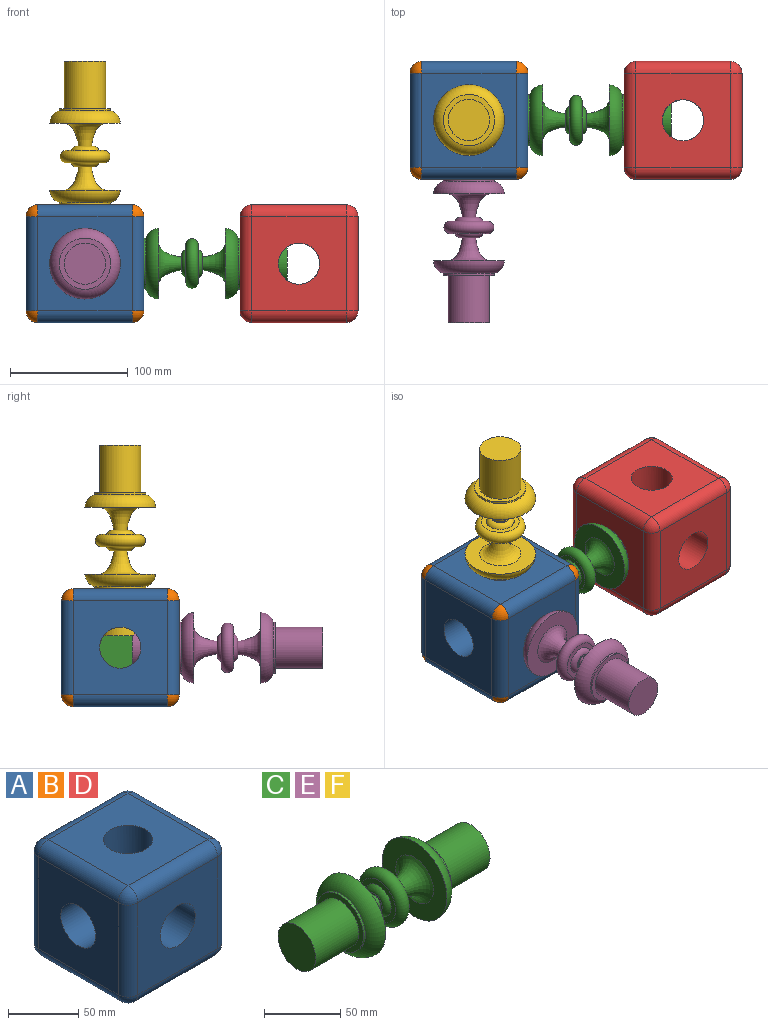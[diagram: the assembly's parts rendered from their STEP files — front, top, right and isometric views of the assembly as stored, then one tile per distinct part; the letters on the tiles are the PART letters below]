
ASSEMBLY  parts=6 mates=4
PART A: 32 faces, bbox 100x100x100 mm
  f0: cylinder r=17.5mm len=37.63mm, axis (0,-1,0), area 3765.4mm2, adj f5,f8,f9,f10,f11
  f1: plane 80x80mm, normal (1,0,0), area 5437.9mm2, adj f8,f20,f25,f28,f31
  f2: plane 80x80mm, normal (0,0,1), area 5437.9mm2, adj f11,f17,f26,f27,f31
  f3: plane 80x80mm, normal (-1,0,0), area 5437.9mm2, adj f9,f12,f16,f17,f18
  f4: plane 80x80mm, normal (0,0,-1), area 5437.9mm2, adj f10,f12,f15,f19,f20
  f5: plane 80x80mm, normal (0,-1,0), area 5437.9mm2, adj f0,f15,f16,f25,f26
  f6: plane 80x80mm, normal (0,1,0), area 5437.9mm2, adj f7,f18,f19,f27,f28
  f7: cylinder r=17.5mm len=37.63mm, axis (0,-1,0), area 3765.4mm2, adj f6,f8,f9,f10,f11
  f8: cylinder r=17.5mm len=37.63mm, axis (1,0,0), area 3765.4mm2, adj f0,f1,f7,f10,f11
  f9: cylinder r=17.5mm len=37.63mm, axis (1,0,0), area 3765.4mm2, adj f0,f3,f7,f10,f11
  f10: cylinder r=17.5mm len=37.63mm, axis (0,0,1), area 3765.4mm2, adj f0,f4,f7,f8,f9
  f11: cylinder r=17.5mm len=37.63mm, axis (0,0,1), area 3765.4mm2, adj f0,f2,f7,f8,f9
  f12: cylinder r=10mm len=80mm, axis (0,1,0), area 1256.6mm2, adj f3,f4,f13,f14
  f13: sphere r=10mm, area 157.1mm2, adj f12,f15,f16
  f14: sphere r=10mm, area 157.1mm2, adj f12,f18,f19
  f15: cylinder r=10mm len=80mm, axis (-1,0,0), area 1256.6mm2, adj f4,f5,f13,f21
  f16: cylinder r=10mm len=80mm, axis (0,0,1), area 1256.6mm2, adj f3,f5,f13,f22
  f17: cylinder r=10mm len=80mm, axis (0,-1,0), area 1256.6mm2, adj f2,f3,f22,f23
  f18: cylinder r=10mm len=80mm, axis (0,0,-1), area 1256.6mm2, adj f3,f6,f14,f23
  f19: cylinder r=10mm len=80mm, axis (1,0,0), area 1256.6mm2, adj f4,f6,f14,f24
  f20: cylinder r=10mm len=80mm, axis (0,-1,0), area 1256.6mm2, adj f1,f4,f21,f24
  f21: sphere r=10mm, area 157.1mm2, adj f15,f20,f25
  f22: sphere r=10mm, area 157.1mm2, adj f16,f17,f26
  f23: sphere r=10mm, area 157.1mm2, adj f17,f18,f27
  f24: sphere r=10mm, area 157.1mm2, adj f19,f20,f28
  f25: cylinder r=10mm len=80mm, axis (0,0,-1), area 1256.6mm2, adj f1,f5,f21,f29
  f26: cylinder r=10mm len=80mm, axis (1,0,0), area 1256.6mm2, adj f2,f5,f22,f29
  f27: cylinder r=10mm len=80mm, axis (-1,0,0), area 1256.6mm2, adj f2,f6,f23,f30
  f28: cylinder r=10mm len=80mm, axis (0,0,1), area 1256.6mm2, adj f1,f6,f24,f30
  f29: sphere r=10mm, area 157.1mm2, adj f25,f26,f31
  f30: sphere r=10mm, area 157.1mm2, adj f27,f28,f31
  f31: cylinder r=10mm len=80mm, axis (0,1,0), area 1256.6mm2, adj f1,f2,f29,f30
PART B: same geometry as A
PART C: 21 faces, bbox 161.6x65x65 mm
  f0: cylinder r=21.71mm len=43.42mm, axis (-1,0,0), area 235.7mm2, adj f1,f9
  f1: torus R=18.51mm, axis (-1,0,0), area 2448mm2, adj f0,f2
  f2: plane 60x60mm, normal (-1,0,0), area 1865.3mm2, adj f1,f3
  f3: revolved ~35x35mm, area 1486.7mm2, adj f2,f4
  f4: plane 14.12x14.12mm, normal (1,0,0), area 58.4mm2, adj f3,f20
  f5: plane 31.94x31.94mm, normal (1,0,0), area 360.9mm2, adj f6,f20
  f6: torus R=15.97mm, axis (-1,0,0), area 1993.2mm2, adj f5,f15
  f7: plane 35x35mm, normal (1,0,0), area 962.1mm2, adj f8
  f8: cylinder r=17.5mm len=40mm, axis (-1,0,0), area 4398.2mm2, adj f7,f9
  f9: plane 43.42x43.42mm, normal (1,0,0), area 518.3mm2, adj f0,f8
  f10: cylinder r=21.71mm len=43.42mm, axis (1,0,0), area 235.7mm2, adj f11,f18
  f11: torus R=18.51mm, axis (1,0,0), area 2448mm2, adj f10,f12
  f12: plane 60x60mm, normal (1,0,0), area 1865.3mm2, adj f11,f13
  f13: revolved ~35x35mm, area 1486.7mm2, adj f12,f14
  f14: plane 14.12x14.12mm, normal (-1,0,0), area 58.4mm2, adj f13,f19
  f15: plane 31.94x31.94mm, normal (-1,0,0), area 360.9mm2, adj f6,f19
  f16: plane 35x35mm, normal (-1,0,0), area 962.1mm2, adj f17
  f17: cylinder r=17.5mm len=40mm, axis (1,0,0), area 4398.2mm2, adj f16,f18
  f18: plane 43.42x43.42mm, normal (-1,0,0), area 518.3mm2, adj f10,f17
  f19: torus R=7.06mm, axis (1,0,0), area 393.4mm2, adj f14,f15
  f20: torus R=7.06mm, axis (-1,0,0), area 393.4mm2, adj f4,f5
PART D: same geometry as A
PART E: same geometry as C
PART F: same geometry as C
PLACE A t=(0.18,0.27,0.25)mm
PLACE B t=(0.18,0.27,0.25)mm fixed
PLACE C t=(90.96,0.27,0.25)mm
PLACE D rot(axis=(0,-1,0),90deg) t=(181.74,0.27,0.25)mm
PLACE E rot(axis=(-0.71,-0.71,0),180deg) t=(0.18,-90.52,0.25)mm
PLACE F rot(axis=(0,1,0),90deg) t=(0.18,0.27,91.03)mm
MATE fastened B.f0 <-> E.f0  axis (0,-1,0) through (0.18,-49.73,0.25)mm
MATE fastened B.f10 <-> F.f0  axis (0,0,1) through (0.18,0.27,50.25)mm
MATE fastened B.f8 <-> C.f0  axis (1,0,0) through (50.18,0.27,0.25)mm
MATE fastened C.f0 <-> D.f10  axis (1,0,0) through (131.74,0.27,0.25)mm
